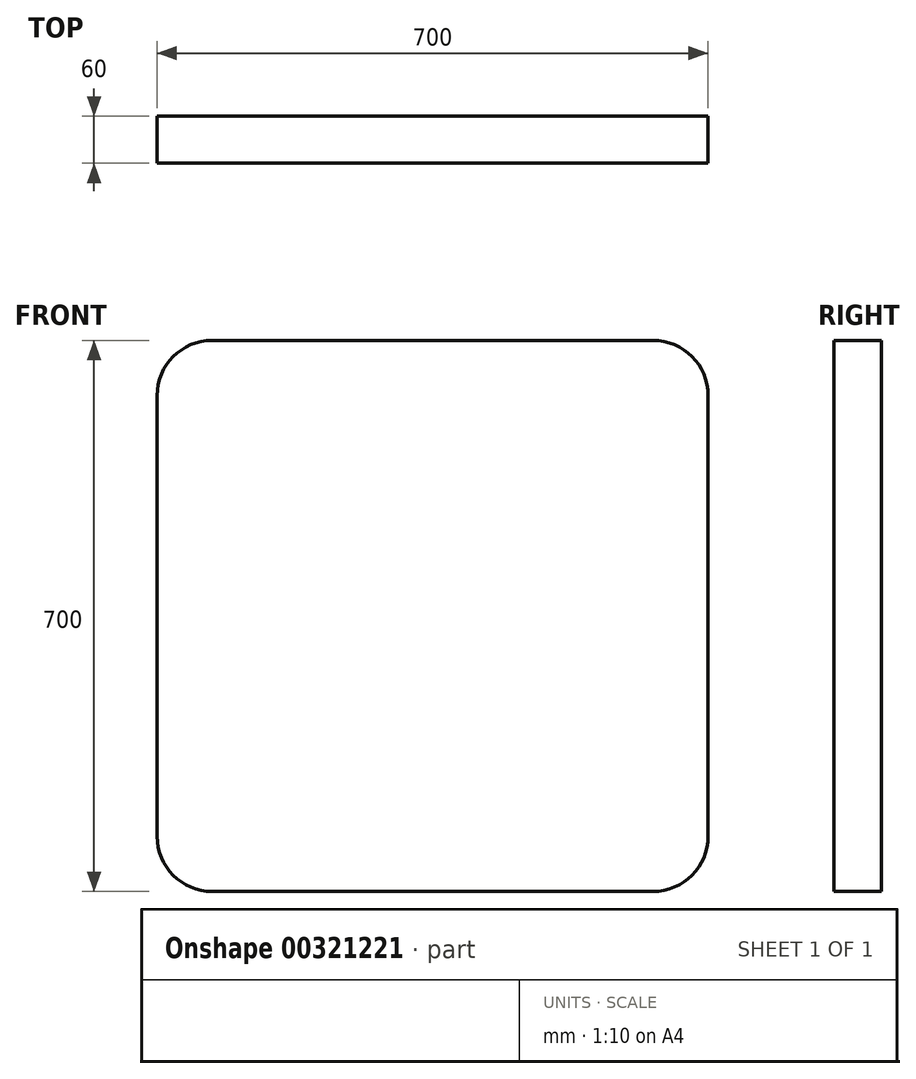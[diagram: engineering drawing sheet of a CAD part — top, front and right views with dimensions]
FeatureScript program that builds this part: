
annotation { "Feature Type Name" : "Feature", "Feature Type Description" : "" }
export const myFeature = defineFeature(function(context is Context, id is Id, definition is map)
    precondition{}
    {
        {
            var Q0;
            Q0=qCreatedBy(makeId("Front.planeOp"),FACE);
            var sketch = newSketch(context, id + "F0", { "sketchPlane" : qUnion([Q0])});
            skLineSegment(sketch, "E0", {"start": v(0, 0) * mm, "end": v(700, 0) * mm});
            skLineSegment(sketch, "E1", {"start": v(700, 0) * mm, "end": v(700, -700) * mm});
            skLineSegment(sketch, "E2", {"start": v(700, -700) * mm, "end": v(0, -700) * mm});
            skLineSegment(sketch, "E3", {"start": v(0, -700) * mm, "end": v(0, 0) * mm});
            skSolve(sketch);
        }
        {
            var Q0;
            Q0 = qSketchRegion(id + "F0", true);
            extrude(context, id + "F1", {"entities" : qUnion([Q0]), "depth" : 60 * mm});
        }
        {
            var Q0;
            Q0=makeQuery(id+"F1.opExtrude","SWEPT_EDGE",EDGE,{"disambiguationData":[OSD([sQuery(id+"F0.wireOp",EDGE,"E0"),sQuery(id+"F0.wireOp",EDGE,"E1")])]});
            var Q1;
            Q1=makeQuery(id+"F1.opExtrude","SWEPT_EDGE",EDGE,{"disambiguationData":[OSD([sQuery(id+"F0.wireOp",EDGE,"E1"),sQuery(id+"F0.wireOp",EDGE,"E2")])]});
            var Q2;
            Q2=makeQuery(id+"F1.opExtrude","SWEPT_EDGE",EDGE,{"disambiguationData":[OSD([sQuery(id+"F0.wireOp",EDGE,"E2"),sQuery(id+"F0.wireOp",EDGE,"E3")])]});
            var Q3;
            Q3=makeQuery(id+"F1.opExtrude","SWEPT_EDGE",EDGE,{"disambiguationData":[OSD([sQuery(id+"F0.wireOp",EDGE,"E0"),sQuery(id+"F0.wireOp",EDGE,"E3")])]});
            fillet(context, id + "F2", {"entities" : qUnion([Q0, Q1, Q2, Q3]), "radius" : 70 * mm, "tangentPropagation" : true, "allowEdgeOverflow" : false});
        }
    });
